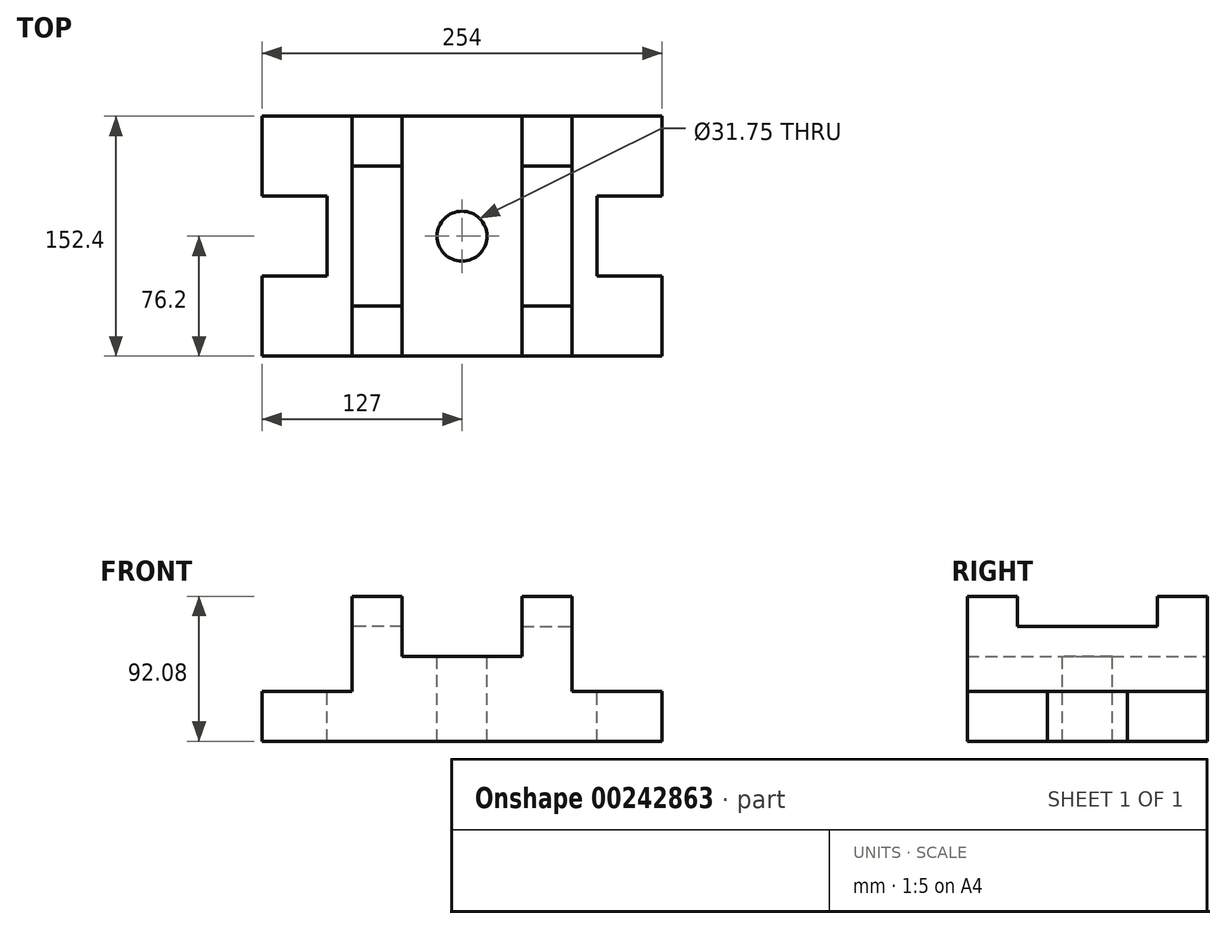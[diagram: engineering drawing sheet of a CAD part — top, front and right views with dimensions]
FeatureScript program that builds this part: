
annotation { "Feature Type Name" : "Feature", "Feature Type Description" : "" }
export const myFeature = defineFeature(function(context is Context, id is Id, definition is map)
    precondition{}
    {
        {
            var Q0;
            Q0=qCreatedBy(makeId("Front.planeOp"),FACE);
            var sketch = newSketch(context, id + "F0", { "sketchPlane" : qUnion([Q0])});
            skLineSegment(sketch, "E0", {"start": v(-38.1, 0) * mm, "end": v(38.1, 0) * mm});
            skLineSegment(sketch, "E1", {"start": v(38.1, 0) * mm, "end": v(38.1, 38.1) * mm});
            skLineSegment(sketch, "E2", {"start": v(38.1, 38.1) * mm, "end": v(69.85, 38.1) * mm});
            skLineSegment(sketch, "E3", {"start": v(69.85, 38.1) * mm, "end": v(69.85, -22.23) * mm});
            skLineSegment(sketch, "E4", {"start": v(69.85, -22.23) * mm, "end": v(127, -22.23) * mm});
            skLineSegment(sketch, "E5", {"start": v(127, -22.23) * mm, "end": v(127, -53.98) * mm});
            skLineSegment(sketch, "E6", {"start": v(127, -53.98) * mm, "end": v(0, -53.98) * mm});
            skLineSegment(sketch, "E7", {"start": v(0, -53.98) * mm, "end": v(-127, -53.98) * mm});
            skLineSegment(sketch, "E8", {"start": v(-127, -53.98) * mm, "end": v(-127, -22.23) * mm});
            skLineSegment(sketch, "E9", {"start": v(-127, -22.23) * mm, "end": v(-69.85, -22.23) * mm});
            skLineSegment(sketch, "E10", {"start": v(-69.85, -22.23) * mm, "end": v(-69.85, 38.1) * mm});
            skLineSegment(sketch, "E11", {"start": v(-69.85, 38.1) * mm, "end": v(-38.1, 38.1) * mm});
            skLineSegment(sketch, "E12", {"start": v(-38.1, 38.1) * mm, "end": v(-38.1, 0) * mm});
            skSolve(sketch);
        }
        {
            var Q0;
            Q0=makeQuery(id+"F0.imprint","IMPRINT",FACE,{"disambiguationData":[TD([[makeQuery(id+"F0.imprint","IMPRINT",EDGE,{"derivedFrom":sQuery(id+"F0.wireOp",EDGE,"E0")}),-1.0]])]});
            extrude(context, id + "F1", {"entities" : qUnion([Q0]), "depth" : 152.4 * mm});
        }
        {
            var Q0;
            Q0=makeQuery(id+"F1.opExtrude","SWEPT_FACE",FACE,{"disambiguationData":[OSD([sQuery(id+"F0.wireOp",EDGE,"E4")])]});
            var sketch = newSketch(context, id + "F2", { "sketchPlane" : qUnion([Q0])});
            skLineSegment(sketch, "E13", {"start": v(127, -101.6) * mm, "end": v(85.72, -101.6) * mm});
            skLineSegment(sketch, "E14", {"start": v(85.72, -101.6) * mm, "end": v(85.72, -50.8) * mm});
            skLineSegment(sketch, "E15", {"start": v(85.72, -50.8) * mm, "end": v(127, -50.8) * mm});
            skSolve(sketch);
        }
        {
            var Q0;
            {var subQ0=sQuery(id+"F2.wireOp",EDGE,"E13");Q0=makeQuery(id+"F2.imprint","IMPRINT",FACE,{"disambiguationData":[TD([[makeQuery(id+"F2.imprint","IMPRINT",EDGE,{"derivedFrom":subQ0}),-1.0]])]});}
            extrude(context, id + "F3", {"entities" : qUnion([Q0]), "operationType" : NewBodyOperationType.REMOVE, "oppositeDirection" : true, "depth" : 76.2 * mm});
        }
        {
            var Q0;
            Q0=makeQuery(id+"F1.opExtrude","SWEPT_FACE",FACE,{"disambiguationData":[OSD([sQuery(id+"F0.wireOp",EDGE,"E9")])]});
            var sketch = newSketch(context, id + "F4", { "sketchPlane" : qUnion([Q0])});
            skLineSegment(sketch, "E16", {"start": v(-127, -50.8) * mm, "end": v(-85.72, -50.8) * mm});
            skLineSegment(sketch, "E17", {"start": v(-85.72, -50.8) * mm, "end": v(-85.72, -101.6) * mm});
            skLineSegment(sketch, "E18", {"start": v(-85.72, -101.6) * mm, "end": v(-127, -101.6) * mm});
            skSolve(sketch);
        }
        {
            var Q0;
            {var subQ0=sQuery(id+"F4.wireOp",EDGE,"E16");Q0=makeQuery(id+"F4.imprint","IMPRINT",FACE,{"disambiguationData":[TD([[makeQuery(id+"F4.imprint","IMPRINT",EDGE,{"derivedFrom":subQ0}),-1.0]])]});}
            extrude(context, id + "F5", {"entities" : qUnion([Q0]), "operationType" : NewBodyOperationType.REMOVE, "oppositeDirection" : true, "depth" : 76.2 * mm});
        }
        {
            var Q0;
            Q0=makeQuery(id+"F1.opExtrude","SWEPT_FACE",FACE,{"disambiguationData":[OSD([sQuery(id+"F0.wireOp",EDGE,"E10")])]});
            var sketch = newSketch(context, id + "F6", { "sketchPlane" : qUnion([Q0])});
            skLineSegment(sketch, "E19", {"start": v(31.75, 38.1) * mm, "end": v(31.75, 19.05) * mm});
            skLineSegment(sketch, "E20", {"start": v(31.75, 19.05) * mm, "end": v(120.65, 19.05) * mm});
            skLineSegment(sketch, "E21", {"start": v(120.65, 19.05) * mm, "end": v(120.65, 38.1) * mm});
            skSolve(sketch);
        }
        {
            var Q0;
            {var subQ0=sQuery(id+"F6.wireOp",EDGE,"E19");Q0=makeQuery(id+"F6.imprint","IMPRINT",FACE,{"disambiguationData":[TD([[makeQuery(id+"F6.imprint","IMPRINT",EDGE,{"derivedFrom":subQ0}),1.0]])]});}
            extrude(context, id + "F7", {"entities" : qUnion([Q0]), "operationType" : NewBodyOperationType.REMOVE, "oppositeDirection" : true, "depth" : 50.8 * mm});
        }
        {
            var Q0;
            Q0=makeQuery(id+"F1.opExtrude","SWEPT_FACE",FACE,{"disambiguationData":[OSD([sQuery(id+"F0.wireOp",EDGE,"E3")])]});
            var sketch = newSketch(context, id + "F8", { "sketchPlane" : qUnion([Q0])});
            skLineSegment(sketch, "E22", {"start": v(-120.65, 38.1) * mm, "end": v(-120.65, 19.05) * mm});
            skLineSegment(sketch, "E23", {"start": v(-120.65, 19.05) * mm, "end": v(-31.75, 19.05) * mm});
            skLineSegment(sketch, "E24", {"start": v(-31.75, 19.05) * mm, "end": v(-31.75, 38.1) * mm});
            skSolve(sketch);
        }
        {
            var Q0;
            {var subQ0=sQuery(id+"F8.wireOp",EDGE,"E22");Q0=makeQuery(id+"F8.imprint","IMPRINT",FACE,{"disambiguationData":[TD([[makeQuery(id+"F8.imprint","IMPRINT",EDGE,{"derivedFrom":subQ0}),1.0]])]});}
            extrude(context, id + "F9", {"entities" : qUnion([Q0]), "operationType" : NewBodyOperationType.REMOVE, "oppositeDirection" : true, "depth" : 76.2 * mm});
        }
        {
            var Q0;
            Q0=makeQuery(id+"F1.opExtrude","SWEPT_FACE",FACE,{"disambiguationData":[OSD([sQuery(id+"F0.wireOp",EDGE,"E0")])]});
            var sketch = newSketch(context, id + "F10", { "sketchPlane" : qUnion([Q0])});
            skCircle(sketch, "E25", {"center": v(0, -76.2) * mm, "radius": 15.88 * mm});
            skPoint(sketch, "E25.centerSnap0", {"position": v(38.1, -76.2) * mm});
            skSolve(sketch);
        }
        {
            var Q0;
            Q0=makeQuery(id+"F10.imprint","IMPRINT",FACE,{"disambiguationData":[TD([[makeQuery(id+"F10.imprint","IMPRINT",EDGE,{"derivedFrom":sQuery(id+"F10.wireOp",EDGE,"E25")}),1.0]])]});
            extrude(context, id + "F11", {"entities" : qUnion([Q0]), "operationType" : NewBodyOperationType.REMOVE, "oppositeDirection" : true, "depth" : 76.2 * mm});
        }
    });
